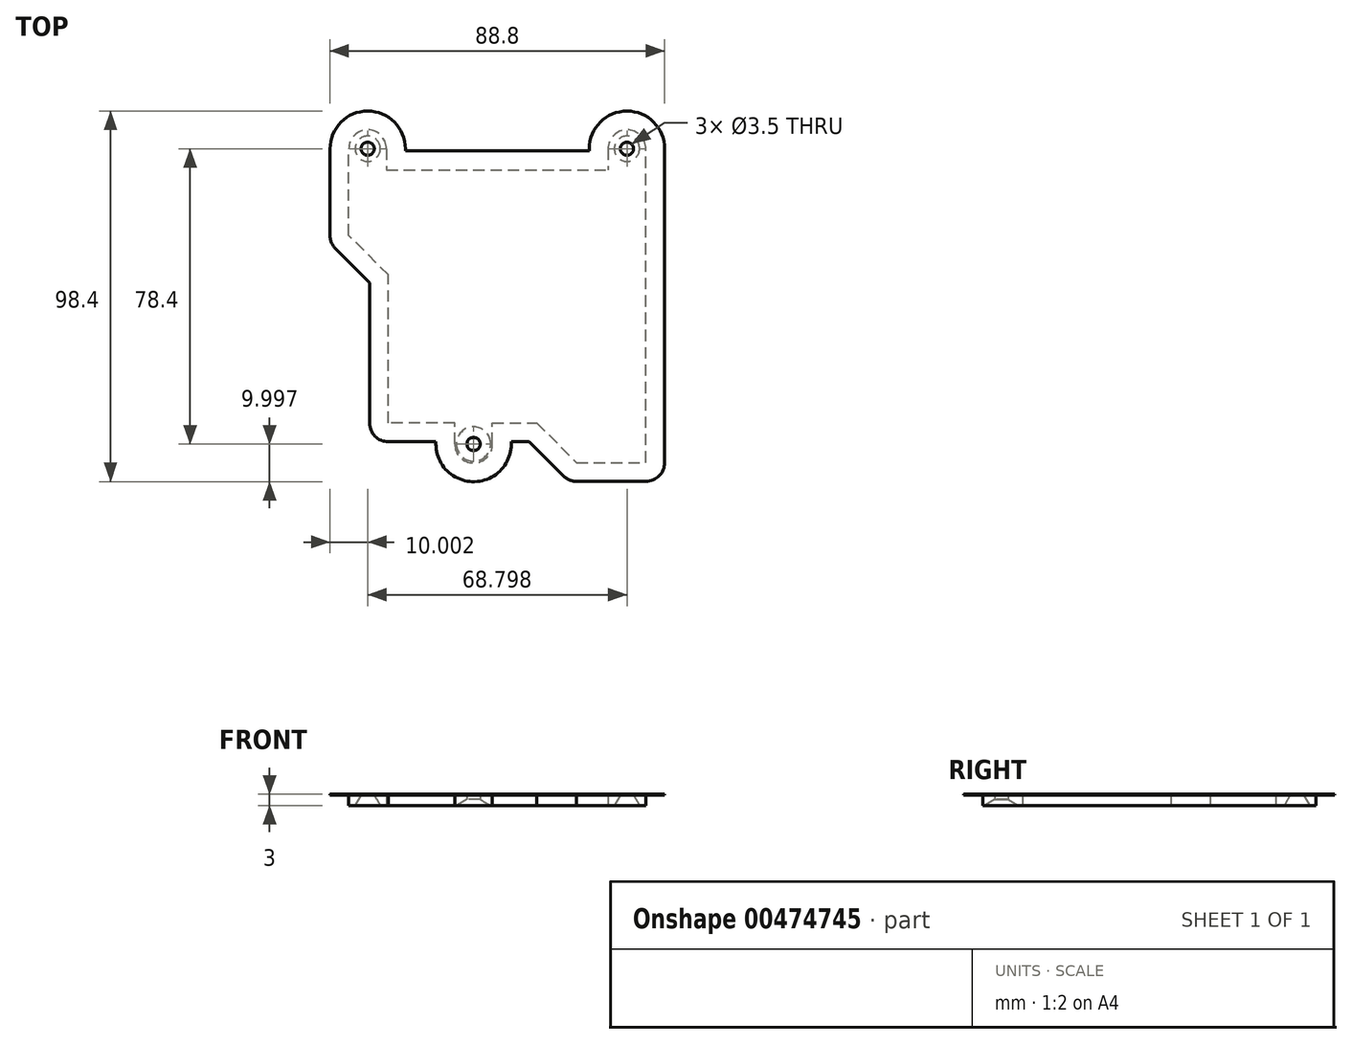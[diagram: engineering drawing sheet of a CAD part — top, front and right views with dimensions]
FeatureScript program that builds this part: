
annotation { "Feature Type Name" : "Feature", "Feature Type Description" : "" }
export const myFeature = defineFeature(function(context is Context, id is Id, definition is map)
    precondition{}
    {
        {
            var Q0;
            Q0=qCreatedBy(makeId("Top.planeOp"),FACE);
            var sketch = newSketch(context, id + "F0", { "sketchPlane" : qUnion([Q0])});
            skLineSegment(sketch, "E0", {"start": v(0, 0) * mm, "end": v(0, -39.5) * mm, "construction": true});
            skLineSegment(sketch, "E1", {"start": v(0, -39.5) * mm, "end": v(17.6, -39.5) * mm, "construction": true});
            skLineSegment(sketch, "E2", {"start": v(39.56, -39.5) * mm, "end": v(50.07, -50) * mm, "construction": true});
            skLineSegment(sketch, "E3", {"start": v(50.07, -50) * mm, "end": v(68.9, -50) * mm, "construction": true});
            skLineSegment(sketch, "E4", {"start": v(68.9, -50) * mm, "end": v(68.9, 33.6) * mm, "construction": true});
            skLineSegment(sketch, "E5", {"start": v(58.3, 28.3) * mm, "end": v(0.1, 28.3) * mm, "construction": true});
            skLineSegment(sketch, "E6", {"start": v(-10.5, 33.6) * mm, "end": v(-10.5, 10.48) * mm, "construction": true});
            skLineSegment(sketch, "E7", {"start": v(-10.5, 10.48) * mm, "end": v(0, 0) * mm, "construction": true});
            skCircle(sketch, "E8", {"center": v(22.9, -44.8) * mm, "radius": 1.4 * mm, "construction": true});
            skCircle(sketch, "E9", {"center": v(-5.2, 33.6) * mm, "radius": 1.4 * mm, "construction": true});
            skCircle(sketch, "E10", {"center": v(63.6, 33.6) * mm, "radius": 1.4 * mm, "construction": true});
            skLineSegment(sketch, "E11", {"start": v(0.1, 28.3) * mm, "end": v(0.1, 33.6) * mm, "construction": true});
            skArc(sketch, "E12", {"start": v(0.1, 33.6) * mm, "mid": v(-5.2, 38.9) * mm, "end": v(-10.5, 33.6) * mm, "construction": true});
            skLineSegment(sketch, "E13", {"start": v(58.3, 28.3) * mm, "end": v(58.3, 33.6) * mm, "construction": true});
            skArc(sketch, "E14", {"start": v(68.9, 33.6) * mm, "mid": v(63.6, 38.9) * mm, "end": v(58.3, 33.6) * mm, "construction": true});
            skLineSegment(sketch, "E15", {"start": v(17.6, -39.5) * mm, "end": v(17.6, -44.8) * mm, "construction": true});
            skLineSegment(sketch, "E16", {"start": v(28.2, -39.5) * mm, "end": v(28.2, -44.8) * mm, "construction": true});
            skArc(sketch, "E17", {"start": v(17.6, -44.8) * mm, "mid": v(22.9, -50.1) * mm, "end": v(28.2, -44.8) * mm, "construction": true});
            skLineSegment(sketch, "E18.trimOffspring", {"start": v(28.2, -39.5) * mm, "end": v(39.56, -39.5) * mm, "construction": true});
            skCircle(sketch, "E19", {"center": v(22.9, -44.8) * mm, "radius": 1.75 * mm});
            skCircle(sketch, "E20", {"center": v(-5.2, 33.6) * mm, "radius": 1.75 * mm});
            skCircle(sketch, "E21", {"center": v(63.6, 33.6) * mm, "radius": 1.75 * mm});
            skLineSegment(sketch, "E22", {"start": v(17.9, -44.8) * mm, "end": v(17.9, -39.2) * mm});
            skLineSegment(sketch, "E23", {"start": v(17.9, -39.2) * mm, "end": v(0.3, -39.2) * mm});
            skLineSegment(sketch, "E24", {"start": v(27.9, -44.8) * mm, "end": v(27.9, -39.2) * mm});
            skArc(sketch, "E25", {"start": v(17.9, -44.8) * mm, "mid": v(22.9, -49.8) * mm, "end": v(27.9, -44.8) * mm});
            skLineSegment(sketch, "E26", {"start": v(0.3, -39.2) * mm, "end": v(0.3, 0.12) * mm});
            skLineSegment(sketch, "E27", {"start": v(0.3, 0.12) * mm, "end": v(-10.2, 10.6) * mm});
            skLineSegment(sketch, "E28", {"start": v(-10.2, 10.6) * mm, "end": v(-10.2, 33.6) * mm});
            skArc(sketch, "E29", {"start": v(-0.2, 33.6) * mm, "mid": v(-5.2, 38.6) * mm, "end": v(-10.2, 33.6) * mm});
            skLineSegment(sketch, "E30", {"start": v(-0.2, 33.6) * mm, "end": v(-0.2, 28) * mm});
            skLineSegment(sketch, "E31", {"start": v(-0.2, 28) * mm, "end": v(58.6, 28) * mm});
            skLineSegment(sketch, "E32", {"start": v(27.9, -39.2) * mm, "end": v(39.68, -39.2) * mm});
            skLineSegment(sketch, "E33", {"start": v(39.68, -39.2) * mm, "end": v(50.2, -49.7) * mm});
            skLineSegment(sketch, "E34", {"start": v(50.2, -49.7) * mm, "end": v(68.6, -49.7) * mm});
            skLineSegment(sketch, "E35", {"start": v(68.6, -49.7) * mm, "end": v(68.6, 33.6) * mm});
            skArc(sketch, "E36", {"start": v(68.6, 33.6) * mm, "mid": v(63.6, 38.6) * mm, "end": v(58.6, 33.6) * mm});
            skLineSegment(sketch, "E37", {"start": v(58.6, 33.6) * mm, "end": v(58.6, 28) * mm});
            skSolve(sketch);
        }
        {
            var Q0;
            Q0=qSketchRegion(id+"F0",true);
            extrude(context, id + "F1", {"entities" : qUnion([Q0]), "depth" : 3 * mm, "offsetDistance" : 25 * mm});
        }
        {
            var Q0;
            Q0=makeQuery(id+"F1.opExtrude","CAP_EDGE",EDGE,{"disambiguationData":[OSD([sQuery(id+"F0.wireOp",EDGE,"E19")])],"isStart":true});
            var Q1;
            Q1=makeQuery(id+"F1.opExtrude","CAP_EDGE",EDGE,{"disambiguationData":[OSD([sQuery(id+"F0.wireOp",EDGE,"E20")])],"isStart":true});
            var Q2;
            Q2=makeQuery(id+"F1.opExtrude","CAP_EDGE",EDGE,{"disambiguationData":[OSD([sQuery(id+"F0.wireOp",EDGE,"E21")])],"isStart":true});
            chamfer(context, id + "F2", {"entities" : qUnion([Q0, Q1, Q2]), "chamferType" : ChamferType.TWO_OFFSETS, "width1" : 1.6 * mm, "oppositeDirection" : false, "width2" : 2.8 * mm, "tangentPropagation" : true});
        }
        {
            var Q0;
            Q0=makeQuery(id+"F1.opExtrude","CAP_FACE",FACE,{"disambiguationData":[OSD([sQuery(id+"F0.wireOp",EDGE,"E19"),sQuery(id+"F0.wireOp",EDGE,"E20"),sQuery(id+"F0.wireOp",EDGE,"E21"),sQuery(id+"F0.wireOp",EDGE,"E22"),sQuery(id+"F0.wireOp",EDGE,"E23"),sQuery(id+"F0.wireOp",EDGE,"E24"),sQuery(id+"F0.wireOp",EDGE,"E25"),sQuery(id+"F0.wireOp",EDGE,"E26"),sQuery(id+"F0.wireOp",EDGE,"E27"),sQuery(id+"F0.wireOp",EDGE,"E28"),sQuery(id+"F0.wireOp",EDGE,"E29"),sQuery(id+"F0.wireOp",EDGE,"E30"),sQuery(id+"F0.wireOp",EDGE,"E31"),sQuery(id+"F0.wireOp",EDGE,"E32"),sQuery(id+"F0.wireOp",EDGE,"E33"),sQuery(id+"F0.wireOp",EDGE,"E34"),sQuery(id+"F0.wireOp",EDGE,"E35"),sQuery(id+"F0.wireOp",EDGE,"E36"),sQuery(id+"F0.wireOp",EDGE,"E37")])],"isStart":false});
            var sketch = newSketch(context, id + "F3", { "sketchPlane" : qUnion([Q0])});
            skLineSegment(sketch, "E38", {"start": v(-10.2, 10.6) * mm, "end": v(0.3, 0.12) * mm});
            skLineSegment(sketch, "E39", {"start": v(0.3, 0.12) * mm, "end": v(0.3, -39.2) * mm});
            skLineSegment(sketch, "E40", {"start": v(0.3, -39.2) * mm, "end": v(17.9, -39.2) * mm});
            skLineSegment(sketch, "E41", {"start": v(17.9, -39.2) * mm, "end": v(17.9, -44.8) * mm});
            skArc(sketch, "E42", {"start": v(17.9, -44.8) * mm, "mid": v(22.9, -49.8) * mm, "end": v(27.9, -44.8) * mm});
            skLineSegment(sketch, "E43", {"start": v(27.9, -44.8) * mm, "end": v(27.9, -39.2) * mm});
            skLineSegment(sketch, "E44", {"start": v(27.9, -39.2) * mm, "end": v(39.68, -39.2) * mm});
            skLineSegment(sketch, "E45", {"start": v(39.68, -39.2) * mm, "end": v(50.2, -49.7) * mm});
            skLineSegment(sketch, "E46", {"start": v(50.2, -49.7) * mm, "end": v(68.6, -49.7) * mm});
            skLineSegment(sketch, "E47", {"start": v(68.6, -49.7) * mm, "end": v(68.6, 33.6) * mm});
            skLineSegment(sketch, "E48", {"start": v(-10.2, 33.6) * mm, "end": v(-10.2, 10.6) * mm});
            skLineSegment(sketch, "E49", {"start": v(-0.2, 33.6) * mm, "end": v(-0.2, 28) * mm});
            skLineSegment(sketch, "E50", {"start": v(-0.2, 28) * mm, "end": v(58.6, 28) * mm});
            skLineSegment(sketch, "E51", {"start": v(58.6, 28) * mm, "end": v(58.6, 33.6) * mm});
            skArc(sketch, "E52", {"start": v(-0.2, 33.6) * mm, "mid": v(-5.2, 38.6) * mm, "end": v(-10.2, 33.6) * mm});
            skArc(sketch, "E53", {"start": v(68.6, 33.6) * mm, "mid": v(63.6, 38.6) * mm, "end": v(58.6, 33.6) * mm});
            skLineSegment(sketch, "E54", {"start": v(-15.2, 33.6) * mm, "end": v(-15.2, 10.6) * mm});
            skLineSegment(sketch, "E55", {"start": v(-13.73, 7.07) * mm, "end": v(-4.7, -1.95) * mm});
            skLineSegment(sketch, "E56", {"start": v(-4.7, -1.95) * mm, "end": v(-4.7, -39.2) * mm});
            skLineSegment(sketch, "E57", {"start": v(0.3, -44.2) * mm, "end": v(12.9, -44.2) * mm});
            skLineSegment(sketch, "E58", {"start": v(12.9, -44.2) * mm, "end": v(12.9, -44.8) * mm});
            skArc(sketch, "E59", {"start": v(12.9, -44.8) * mm, "mid": v(23.2, -54.79) * mm, "end": v(32.88, -44.2) * mm});
            skArc(sketch, "E60", {"start": v(-4.7, -39.2) * mm, "mid": v(-3.24, -42.73) * mm, "end": v(0.3, -44.2) * mm});
            skArc(sketch, "E61", {"start": v(-15.2, 10.6) * mm, "mid": v(-14.82, 8.69) * mm, "end": v(-13.73, 7.07) * mm});
            skLineSegment(sketch, "E62", {"start": v(32.88, -44.2) * mm, "end": v(37.61, -44.2) * mm});
            skLineSegment(sketch, "E63", {"start": v(37.61, -44.2) * mm, "end": v(46.66, -53.23) * mm});
            skLineSegment(sketch, "E64", {"start": v(50.2, -54.7) * mm, "end": v(68.6, -54.7) * mm});
            skArc(sketch, "E65", {"start": v(46.66, -53.23) * mm, "mid": v(48.29, -54.31) * mm, "end": v(50.2, -54.7) * mm});
            skLineSegment(sketch, "E66", {"start": v(73.6, 33.6) * mm, "end": v(73.6, -49.7) * mm});
            skArc(sketch, "E67", {"start": v(68.6, -54.7) * mm, "mid": v(72.14, -53.23) * mm, "end": v(73.6, -49.7) * mm});
            skArc(sketch, "E68", {"start": v(73.6, 33.6) * mm, "mid": v(63.6, 43.6) * mm, "end": v(53.6, 33.6) * mm});
            skArc(sketch, "E69", {"start": v(4.8, 33.6) * mm, "mid": v(-5.2, 43.6) * mm, "end": v(-15.2, 33.6) * mm});
            skLineSegment(sketch, "E70", {"start": v(4.8, 33.6) * mm, "end": v(4.8, 33) * mm});
            skLineSegment(sketch, "E71", {"start": v(4.8, 33) * mm, "end": v(53.6, 33) * mm});
            skLineSegment(sketch, "E72", {"start": v(53.6, 33) * mm, "end": v(53.6, 33.6) * mm});
            skSolve(sketch);
        }
        {
            var Q0;
            Q0 = qSketchRegion(id + "F3", true);
            extrude(context, id + "F4", {"entities" : qUnion([Q0]), "operationType" : NewBodyOperationType.ADD, "oppositeDirection" : true, "depth" : 0.2 * mm, "offsetDistance" : 25 * mm});
        }
    });
